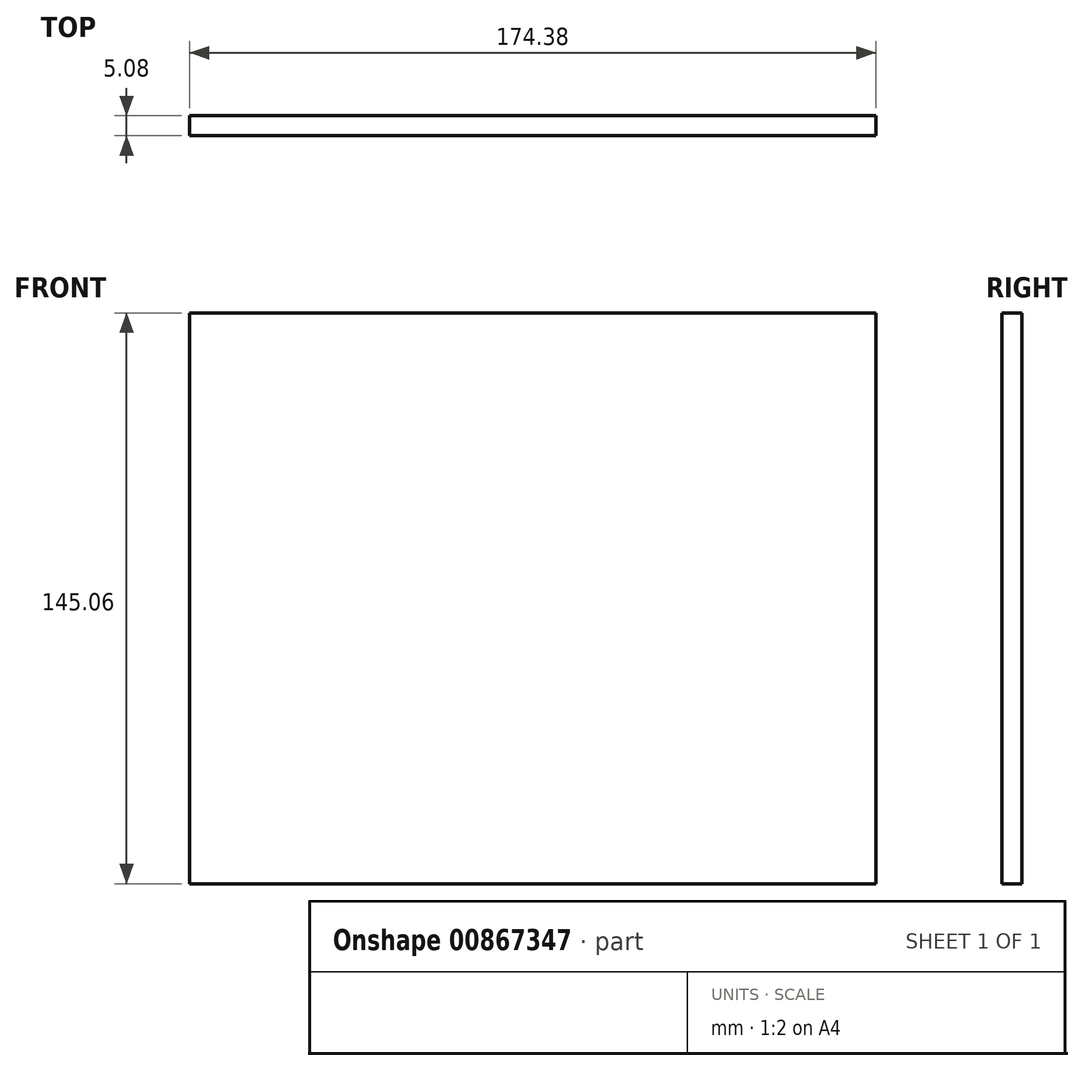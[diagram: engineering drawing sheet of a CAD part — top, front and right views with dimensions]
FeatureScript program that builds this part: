
annotation { "Feature Type Name" : "Feature", "Feature Type Description" : "" }
export const myFeature = defineFeature(function(context is Context, id is Id, definition is map)
    precondition{}
    {
        {
            var Q0;
            Q0=qCreatedBy(makeId("Front.planeOp"),FACE);
            var sketch = newSketch(context, id + "F0", { "sketchPlane" : qUnion([Q0])});
            skLineSegment(sketch, "E0.bottom", {"start": v(-87.19, 72.53) * mm, "end": v(87.19, 72.53) * mm});
            skLineSegment(sketch, "E0.top", {"start": v(-87.19, -72.53) * mm, "end": v(87.19, -72.53) * mm});
            skLineSegment(sketch, "E0.left", {"start": v(-87.19, 72.53) * mm, "end": v(-87.19, -72.53) * mm});
            skLineSegment(sketch, "E0.right", {"start": v(87.19, 72.53) * mm, "end": v(87.19, -72.53) * mm});
            skPoint(sketch, "E0.middle", {"position": v(0, 0) * mm});
            skSolve(sketch);
        }
        {
            var Q0;
            Q0 = qSketchRegion(id + "F0", true);
            extrude(context, id + "F1", {"entities" : qUnion([Q0]), "depth" : 5.08 * mm, "offsetDistance" : 25.4 * mm});
        }
    });
